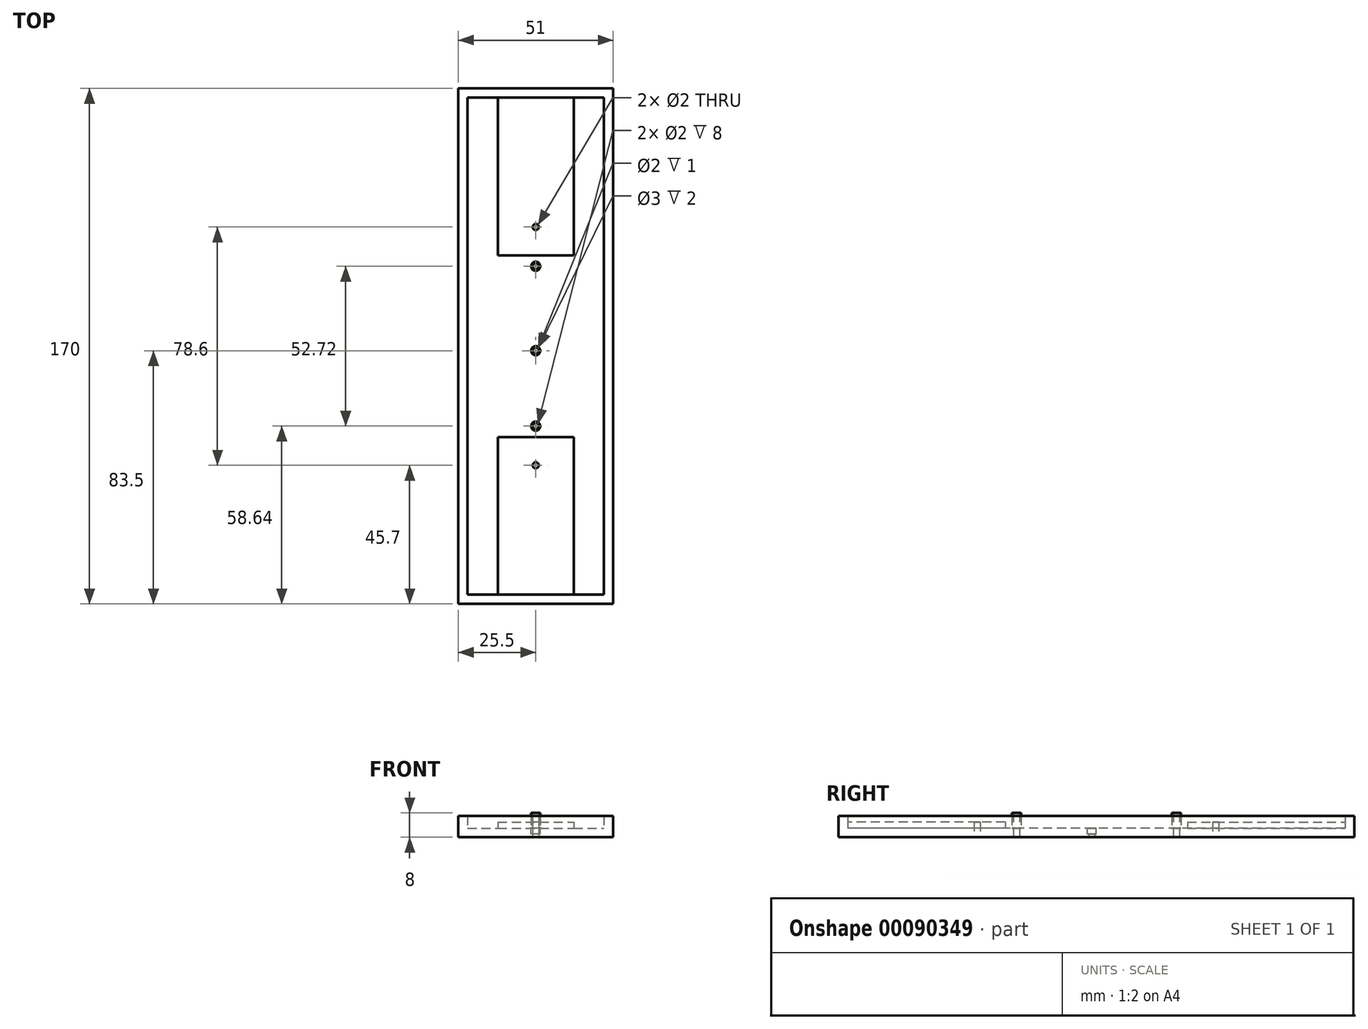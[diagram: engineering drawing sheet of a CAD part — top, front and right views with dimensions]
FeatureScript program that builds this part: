
annotation { "Feature Type Name" : "Feature", "Feature Type Description" : "" }
export const myFeature = defineFeature(function(context is Context, id is Id, definition is map)
    precondition{}
    {
        {
            var Q0;
            Q0=qCreatedBy(makeId("Top.planeOp"),FACE);
            var sketch = newSketch(context, id + "F0", { "sketchPlane" : qUnion([Q0])});
            skLineSegment(sketch, "E0.bottom", {"start": v(0, 0) * mm, "end": v(25, 0) * mm});
            skLineSegment(sketch, "E0.top", {"start": v(0, 52) * mm, "end": v(25, 52) * mm});
            skLineSegment(sketch, "E0.left", {"start": v(0, 0) * mm, "end": v(0, 52) * mm});
            skLineSegment(sketch, "E0.right", {"start": v(25, 0) * mm, "end": v(25, 52) * mm});
            skCircle(sketch, "E1", {"center": v(12.5, 9.3) * mm, "radius": 1 * mm});
            skCircle(sketch, "E2", {"center": v(12.5, -3.64) * mm, "radius": 1.5 * mm});
            skLineSegment(sketch, "E3.bottom", {"start": v(0, -60) * mm, "end": v(25, -60) * mm});
            skLineSegment(sketch, "E3.top", {"start": v(0, -112) * mm, "end": v(25, -112) * mm});
            skLineSegment(sketch, "E3.left", {"start": v(0, -60) * mm, "end": v(0, -112) * mm});
            skLineSegment(sketch, "E3.right", {"start": v(25, -60) * mm, "end": v(25, -112) * mm});
            skCircle(sketch, "E4", {"center": v(12.5, -69.3) * mm, "radius": 1 * mm});
            skPoint(sketch, "E4.centerSnap0", {"position": v(12.5, -60) * mm});
            skCircle(sketch, "E5", {"center": v(12.5, -56.36) * mm, "radius": 1.5 * mm});
            skCircle(sketch, "E6", {"center": v(12.5, -31.5) * mm, "radius": 1.5 * mm});
            skLineSegment(sketch, "E7.bottom", {"start": v(-13, 55) * mm, "end": v(38, 55) * mm});
            skLineSegment(sketch, "E7.top", {"start": v(-13, -115) * mm, "end": v(38, -115) * mm});
            skLineSegment(sketch, "E7.left", {"start": v(-13, 55) * mm, "end": v(-13, -115) * mm});
            skLineSegment(sketch, "E7.right", {"start": v(38, 55) * mm, "end": v(38, -115) * mm});
            skSolve(sketch);
        }
        {
            var Q0;
            Q0=makeQuery(id+"F0.imprint","IMPRINT",FACE,{"disambiguationData":[TD([[makeQuery(id+"F0.imprint","IMPRINT",EDGE,{"derivedFrom":sQuery(id+"F0.wireOp",EDGE,"E3.bottom")}),-1.0]])]});
            var Q1;
            Q1=makeQuery(id+"F0.imprint","IMPRINT",FACE,{"disambiguationData":[TD([[makeQuery(id+"F0.imprint","IMPRINT",EDGE,{"derivedFrom":sQuery(id+"F0.wireOp",EDGE,"E0.bottom")}),1.0]])]});
            extrude(context, id + "F1", {"entities" : qUnion([Q0, Q1]), "depth" : 2 * mm});
        }
        {
            var Q0;
            Q0 = qSketchRegion(id + "F0", true);
            var Q1;
            Q1=makeQuery(id+"F0.imprint","IMPRINT",FACE,{"disambiguationData":[TD([[makeQuery(id+"F0.imprint","IMPRINT",EDGE,{"derivedFrom":sQuery(id+"F0.wireOp",EDGE,"E3.bottom")}),-1.0]])]});
            var Q2;
            Q2=makeQuery(id+"F0.imprint","IMPRINT",FACE,{"disambiguationData":[TD([[makeQuery(id+"F0.imprint","IMPRINT",EDGE,{"derivedFrom":sQuery(id+"F0.wireOp",EDGE,"E0.bottom")}),1.0]])]});
            extrude(context, id + "F2", {"entities" : qUnion([Q0, Q1, Q2]), "operationType" : NewBodyOperationType.ADD, "oppositeDirection" : true, "depth" : 3 * mm});
        }
        {
            var Q0;
            Q0=makeQuery(id+"F2.opExtrude","CAP_FACE",FACE,{"disambiguationData":[OSD([sQuery(id+"F0.wireOp",EDGE,"E1"),sQuery(id+"F0.wireOp",EDGE,"E2"),sQuery(id+"F0.wireOp",EDGE,"E4"),sQuery(id+"F0.wireOp",EDGE,"E5"),sQuery(id+"F0.wireOp",EDGE,"E6"),sQuery(id+"F0.wireOp",EDGE,"E7.bottom"),sQuery(id+"F0.wireOp",EDGE,"E7.top"),sQuery(id+"F0.wireOp",EDGE,"E7.left"),sQuery(id+"F0.wireOp",EDGE,"E7.right")])],"isStart":true});
            var sketch = newSketch(context, id + "F3", { "sketchPlane" : qUnion([Q0])});
            skLineSegment(sketch, "E8.bottom", {"start": v(-10, 52) * mm, "end": v(35, 52) * mm});
            skLineSegment(sketch, "E8.top", {"start": v(-10, -112) * mm, "end": v(35, -112) * mm});
            skLineSegment(sketch, "E8.left", {"start": v(-10, 52) * mm, "end": v(-10, -112) * mm});
            skLineSegment(sketch, "E8.right", {"start": v(35, 52) * mm, "end": v(35, -112) * mm});
            skSolve(sketch);
        }
        {
            var Q0;
            {var subQ6=sQuery(id+"F3.wireOp",EDGE,"E8.left");Q0=makeQuery(id+"F3.imprint","IMPRINT",FACE,{"disambiguationData":[TD([[makeQuery(id+"F3.imprint","IMPRINT",EDGE,{"derivedFrom":subQ6}),-1.0]])]});}
            extrude(context, id + "F4", {"entities" : qUnion([Q0]), "operationType" : NewBodyOperationType.ADD, "depth" : 4 * mm});
        }
        {
            var Q0;
            Q0=makeQuery(id+"F2.opExtrude","CAP_FACE",FACE,{"disambiguationData":[OSD([sQuery(id+"F0.wireOp",EDGE,"E1"),sQuery(id+"F0.wireOp",EDGE,"E2"),sQuery(id+"F0.wireOp",EDGE,"E4"),sQuery(id+"F0.wireOp",EDGE,"E5"),sQuery(id+"F0.wireOp",EDGE,"E6"),sQuery(id+"F0.wireOp",EDGE,"E7.bottom"),sQuery(id+"F0.wireOp",EDGE,"E7.top"),sQuery(id+"F0.wireOp",EDGE,"E7.left"),sQuery(id+"F0.wireOp",EDGE,"E7.right")])],"isStart":true});
            var sketch = newSketch(context, id + "F5", { "sketchPlane" : qUnion([Q0])});
            skCircle(sketch, "E9", {"center": v(12.5, -3.64) * mm, "radius": 1 * mm});
            skCircle(sketch, "E10", {"center": v(12.5, -31.5) * mm, "radius": 1 * mm});
            skCircle(sketch, "E11", {"center": v(12.5, -56.36) * mm, "radius": 1 * mm});
            skSolve(sketch);
        }
        {
            var Q0;
            Q0=makeQuery(id+"F5.imprint","IMPRINT",FACE,{"disambiguationData":[TD([[makeQuery(id+"F5.imprint","IMPRINT",EDGE,{"derivedFrom":sQuery(id+"F5.wireOp",EDGE,"E9")}),-1.0]])]});
            var Q1;
            Q1=makeQuery(id+"F5.imprint","IMPRINT",FACE,{"disambiguationData":[TD([[makeQuery(id+"F5.imprint","IMPRINT",EDGE,{"derivedFrom":sQuery(id+"F5.wireOp",EDGE,"E10")}),-1.0]])]});
            var Q2;
            Q2=makeQuery(id+"F5.imprint","IMPRINT",FACE,{"disambiguationData":[TD([[makeQuery(id+"F5.imprint","IMPRINT",EDGE,{"derivedFrom":sQuery(id+"F5.wireOp",EDGE,"E11")}),-1.0]])]});
            extrude(context, id + "F6", {"entities" : qUnion([Q0, Q1, Q2]), "operationType" : NewBodyOperationType.ADD, "depth" : 5 * mm, "hasSecondDirection" : true, "secondDirectionOppositeDirection" : true, "secondDirectionDepth" : 3 * mm});
        }
        {
            var Q0;
            Q0=makeQuery(id+"F6.opExtrude","CAP_FACE",FACE,{"disambiguationData":[OSD([sQuery(id+"F0.wireOp",EDGE,"E6"),sQuery(id+"F5.wireOp",EDGE,"E10")])],"isStart":false});
            var sketch = newSketch(context, id + "F7", { "sketchPlane" : qUnion([Q0])});
            skSolve(sketch);
        }
        {
            var Q0;
            Q0=makeQuery(id+"F7.imprint","IMPRINT",FACE,{"disambiguationData":[TD([[makeQuery(id+"F7.imprint","IMPRINT",EDGE,{"derivedFrom":makeQuery(id+"F6.opExtrude","CAP_EDGE",EDGE,{"disambiguationData":[OSD([sQuery(id+"F5.wireOp",EDGE,"E10")])],"isStart":false})}),-1.0]])]});
            extrude(context, id + "F8", {"entities" : qUnion([Q0]), "operationType" : NewBodyOperationType.REMOVE, "oppositeDirection" : true, "depth" : 7 * mm});
        }
    });
